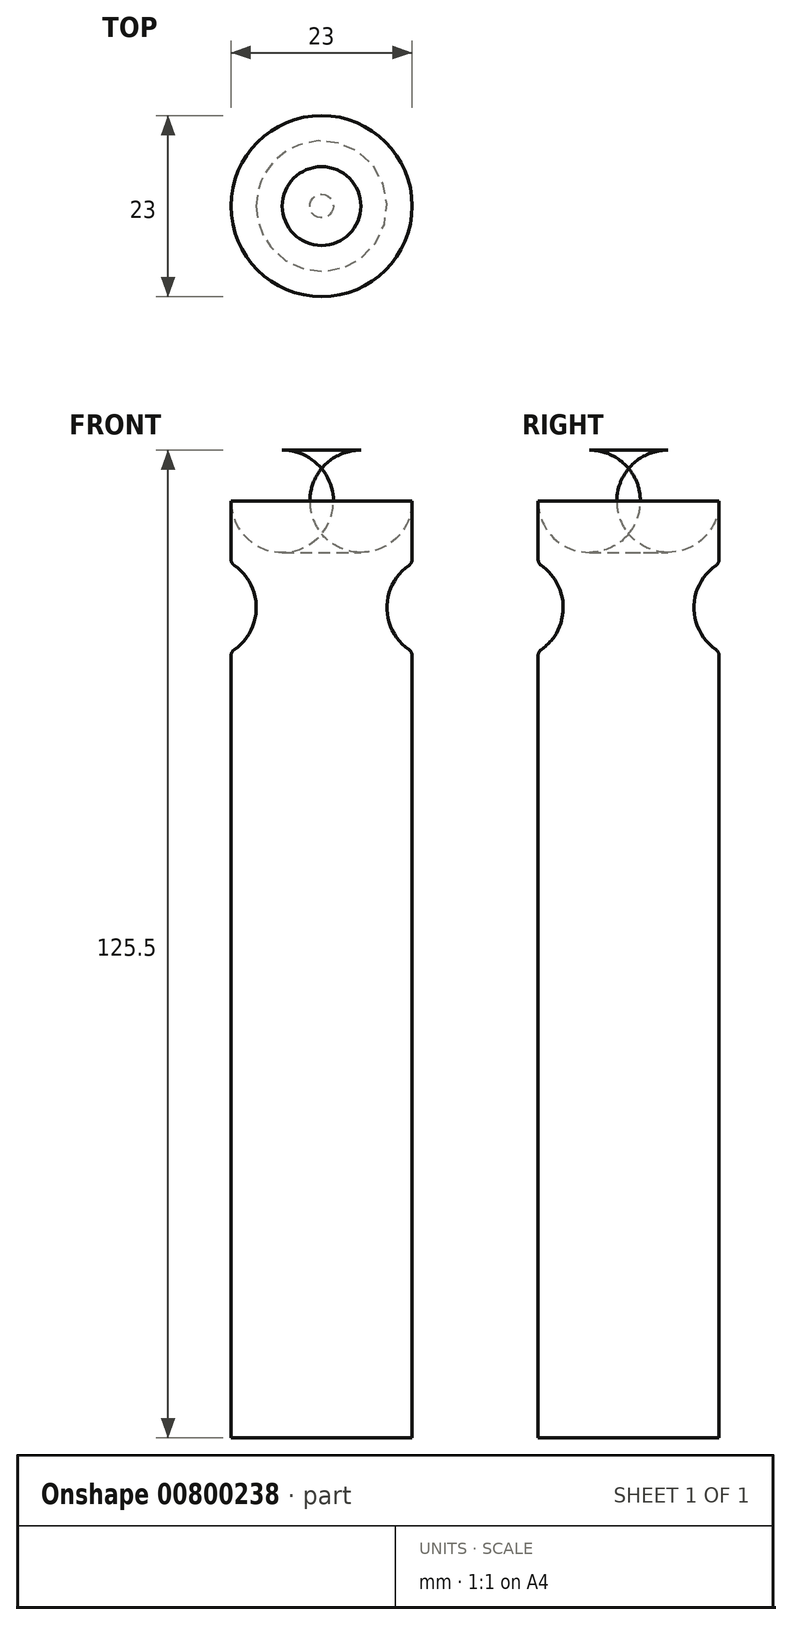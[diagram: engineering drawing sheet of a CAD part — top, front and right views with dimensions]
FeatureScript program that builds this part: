
annotation { "Feature Type Name" : "Feature", "Feature Type Description" : "" }
export const myFeature = defineFeature(function(context is Context, id is Id, definition is map)
    precondition{}
    {
        {
            var Q0;
            Q0=qCreatedBy(makeId("Front.planeOp"),FACE);
            var sketch = newSketch(context, id + "F0", { "sketchPlane" : qUnion([Q0])});
            skLineSegment(sketch, "E0", {"start": v(0, 0) * mm, "end": v(0, 125.5) * mm});
            skLineSegment(sketch, "E1", {"start": v(0, 125.5) * mm, "end": v(-11.5, 125.5) * mm});
            skLineSegment(sketch, "E2", {"start": v(-11.5, 125.5) * mm, "end": v(-11.5, 111) * mm});
            skLineSegment(sketch, "E3", {"start": v(-11.5, 111) * mm, "end": v(-8.3, 111) * mm});
            skLineSegment(sketch, "E4", {"start": v(-8.3, 111) * mm, "end": v(-8.3, 100) * mm});
            skLineSegment(sketch, "E5", {"start": v(-8.3, 100) * mm, "end": v(-11.5, 100) * mm});
            skLineSegment(sketch, "E6", {"start": v(-11.5, 100) * mm, "end": v(-11.5, 0) * mm});
            skLineSegment(sketch, "E7", {"start": v(-11.5, 0) * mm, "end": v(0, 0) * mm});
            skCircle(sketch, "E8", {"center": v(-14.8, 105.5) * mm, "radius": 6.5 * mm});
            skLineSegment(sketch, "E9", {"start": v(-8.3, 105.5) * mm, "end": v(-14.8, 105.5) * mm});
            skSolve(sketch);
        }
        {
            var Q0;
            Q0=makeQuery(id+"F0.imprint","IMPRINT",FACE,{"disambiguationData":[TD([[makeQuery(id+"F0.imprint","IMPRINT",EDGE,{"derivedFrom":sQuery(id+"F0.wireOp",EDGE,"E0")}),1.0]])]});
            var Q1;
            Q1=sQuery(id+"F0.wireOp",EDGE,"E0");
            revolve(context, id + "F1", {"surfaceOperationType" : NewSurfaceOperationType.NEW, "entities" : qUnion([Q0]), "axis" : qUnion([Q1]), "revolveType" : RevolveType.FULL});
        }
        {
            var Q0;
            Q0=makeQuery(id+"F1.opRevolve","SWEPT_EDGE",EDGE,{"disambiguationData":[OSD([sQuery(id+"F0.wireOp",EDGE,"E1"),sQuery(id+"F0.wireOp",EDGE,"E2")])]});
            var Q1;
            Q1=makeQuery(id+"F1.opRevolve","SWEPT_EDGE",EDGE,{"disambiguationData":[OSD([sQuery(id+"F0.wireOp",EDGE,"E3"),sQuery(id+"F0.wireOp",EDGE,"E4")])]});
            var Q2;
            Q2=makeQuery(id+"F1.opRevolve","SWEPT_EDGE",EDGE,{"disambiguationData":[OSD([sQuery(id+"F0.wireOp",EDGE,"E4"),sQuery(id+"F0.wireOp",EDGE,"E5")])]});
            fillet(context, id + "F2", {"entities" : qUnion([Q0, Q1, Q2]), "radius" : 6.5 * mm, "allowEdgeOverflow" : false});
        }
        {
            var Q0;
            Q0=makeQuery(id+"F1.opRevolve","SWEPT_EDGE",EDGE,{"disambiguationData":[OSD([sQuery(id+"F0.wireOp",EDGE,"E2"),sQuery(id+"F0.wireOp",EDGE,"E8")])]});
            var Q1;
            Q1=makeQuery(id+"F1.opRevolve","SWEPT_EDGE",EDGE,{"disambiguationData":[OSD([sQuery(id+"F0.wireOp",EDGE,"E6"),sQuery(id+"F0.wireOp",EDGE,"E8")])]});
            fillet(context, id + "F3", {"entities" : qUnion([Q0, Q1]), "radius" : 1 * mm, "tangentPropagation" : true, "allowEdgeOverflow" : false});
        }
    });
